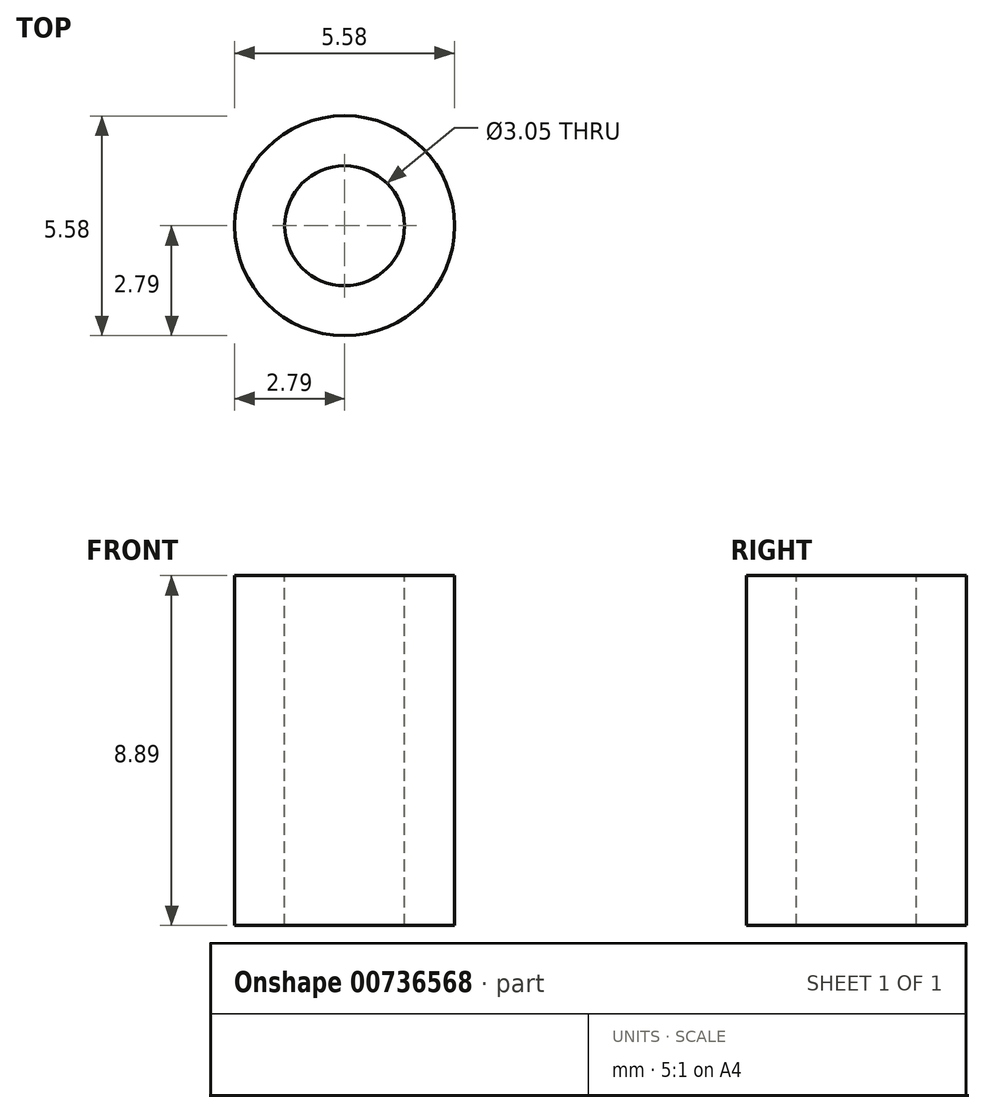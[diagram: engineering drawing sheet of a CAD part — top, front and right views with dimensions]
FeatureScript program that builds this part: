
annotation { "Feature Type Name" : "Feature", "Feature Type Description" : "" }
export const myFeature = defineFeature(function(context is Context, id is Id, definition is map)
    precondition{}
    {
        {
            var Q0;
            Q0=qCreatedBy(makeId("Top.planeOp"),FACE);
            var sketch = newSketch(context, id + "F0", { "sketchPlane" : qUnion([Q0])});
            skCircle(sketch, "E0", {"center": v(0, 0) * mm, "radius": 2.8 * mm});
            skCircle(sketch, "E1.0", {"center": v(0, 0) * mm, "radius": 1.52 * mm});
            skSolve(sketch);
        }
        {
            var Q0;
            Q0 = qSketchRegion(id + "F0", true);
            extrude(context, id + "F1", {"entities" : qUnion([Q0]), "oppositeDirection" : true, "depth" : 8.9 * mm, "offsetDistance" : 25.4 * mm});
        }
    });
